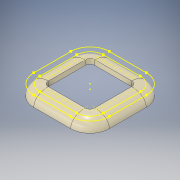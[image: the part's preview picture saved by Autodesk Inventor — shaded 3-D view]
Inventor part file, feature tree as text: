
AUTODESK INVENTOR PART (.ipt)
format: ipt  version: 2018 (Build 220112000, 112)  size: 365,056 bytes
history: native  units: in
note: dims shown in document units (in); Inventor stores cm internally (conversion verified against a paired STEP export)
features: other x15, extrude x2, projected_geometry x1
ambient origin geometry x8: Origin, YZ Plane, XZ Plane, XY Plane, X Axis, Y Axis, Z Axis, Center Point
bodies: Solid1 (feature_tree)
feature tree (18):
  other  "Case Top.ipt"
  other  "East West Opening End-grain Edit"
  other  "North South Opening Long-grain Edit"
  other  "North South inner Long-grain narrowing 1"
  other  "North South inner Long-grain narrowing 2"
  other  "East West inner End-grain widening 1"
  other  "East West inner End-grain widening 2"
  other  "Inner Narrowing Sketch"
  extrude  "Extrusion2"  Depth=0.3937in
  extrude  "Inner Narrowing"  [1 undecoded]
  other  "Solid3::Case Top.ipt"
  other  "TaggingFeature1"
  other  "New peg sketch"
  other  "Alignment Sketch"
  other  "3/16" Vacuum Drill Sketch"
  projected_geometry  "Projected Loop1"
  other  "Size1"
  other  "Size2"
note: 1 required parameter value undecoded (feature->parameter linkage not recoverable at this tier; creation-order binding heuristic only, values carry confidence <= 0.55)
